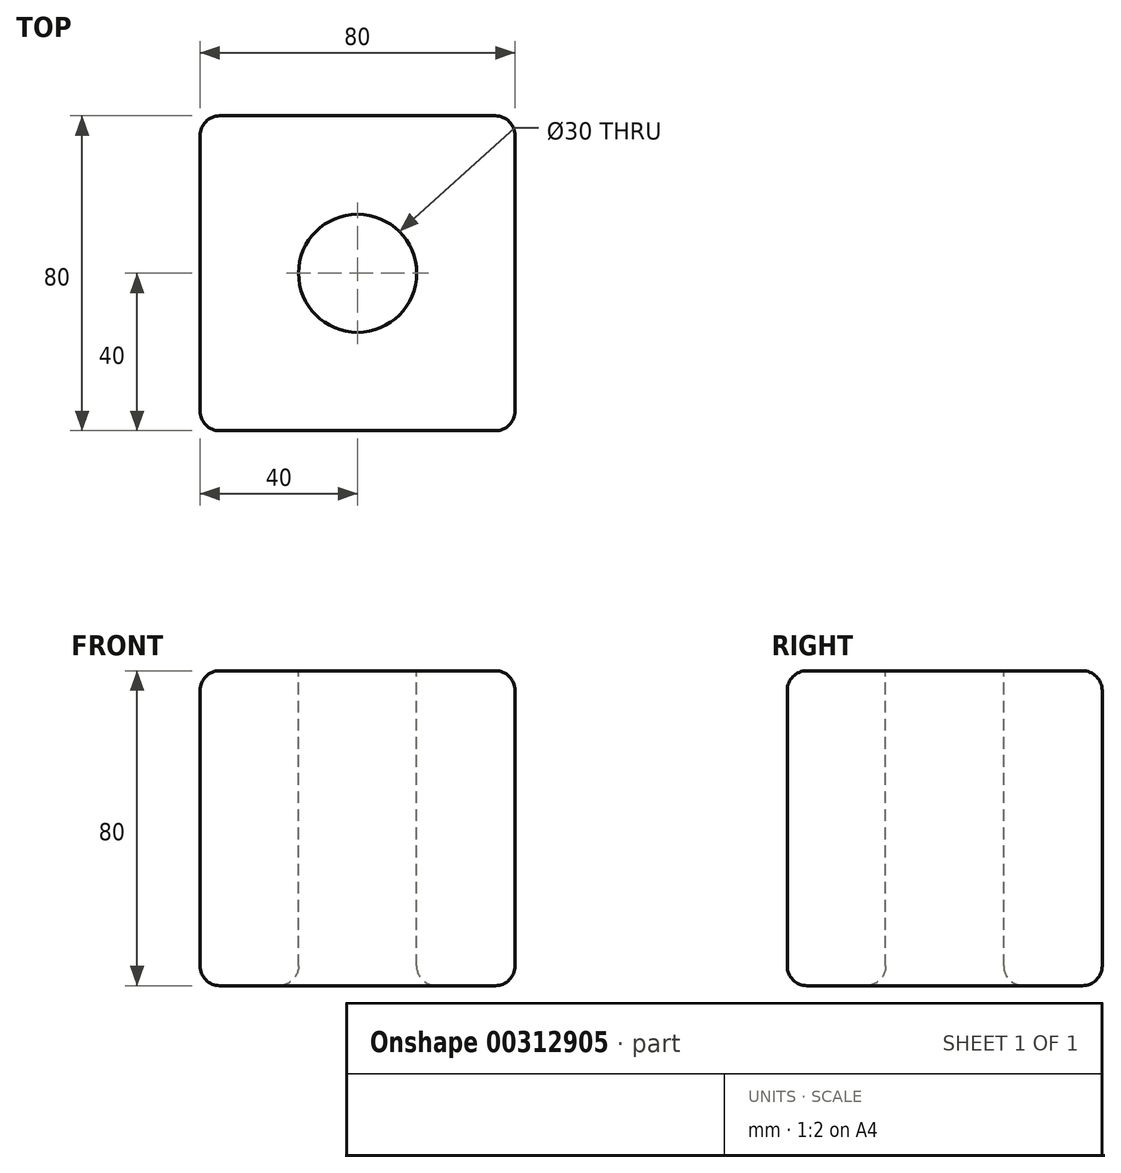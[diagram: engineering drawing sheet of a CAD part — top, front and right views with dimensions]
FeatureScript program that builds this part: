
annotation { "Feature Type Name" : "Feature", "Feature Type Description" : "" }
export const myFeature = defineFeature(function(context is Context, id is Id, definition is map)
    precondition{}
    {
        {
            var Q0;
            Q0=qCreatedBy(makeId("Top.planeOp"),FACE);
            var sketch = newSketch(context, id + "F0", { "sketchPlane" : qUnion([Q0])});
            skLineSegment(sketch, "E0.bottom", {"start": v(-40, 40) * mm, "end": v(40, 40) * mm});
            skLineSegment(sketch, "E0.top", {"start": v(-40, -40) * mm, "end": v(40, -40) * mm});
            skLineSegment(sketch, "E0.left", {"start": v(-40, 40) * mm, "end": v(-40, -40) * mm});
            skLineSegment(sketch, "E0.right", {"start": v(40, 40) * mm, "end": v(40, -40) * mm});
            skPoint(sketch, "E0.middle", {"position": v(0, 0) * mm});
            skSolve(sketch);
        }
        {
            var Q0;
            Q0 = qSketchRegion(id + "F0", true);
            extrude(context, id + "F1", {"entities" : qUnion([Q0]), "endBound" : BoundingType.SYMMETRIC, "depth" : 80 * mm});
        }
        {
            var Q0;
            Q0=makeQuery(id+"F1.opExtrude","CAP_FACE",FACE,{"disambiguationData":[OSD([sQuery(id+"F0.wireOp",EDGE,"E0.bottom"),sQuery(id+"F0.wireOp",EDGE,"E0.top"),sQuery(id+"F0.wireOp",EDGE,"E0.left"),sQuery(id+"F0.wireOp",EDGE,"E0.right")])],"isStart":false});
            var Q1;
            Q1=makeQuery(id+"F1.opExtrude","CAP_EDGE",EDGE,{"disambiguationData":[OSD([sQuery(id+"F0.wireOp",EDGE,"E0.left")])],"isStart":false});
            var Q2;
            Q2=makeQuery(id+"F1.opExtrude","CAP_EDGE",EDGE,{"disambiguationData":[OSD([sQuery(id+"F0.wireOp",EDGE,"E0.top")])],"isStart":false});
            var Q3;
            Q3=makeQuery(id+"F1.opExtrude","CAP_EDGE",EDGE,{"disambiguationData":[OSD([sQuery(id+"F0.wireOp",EDGE,"E0.right")])],"isStart":false});
            var Q4;
            Q4=makeQuery(id+"F1.opExtrude","CAP_EDGE",EDGE,{"disambiguationData":[OSD([sQuery(id+"F0.wireOp",EDGE,"E0.bottom")])],"isStart":false});
            var Q5;
            Q5=makeQuery(id+"F1.opExtrude","SWEPT_EDGE",EDGE,{"disambiguationData":[OSD([sQuery(id+"F0.wireOp",EDGE,"E0.bottom"),sQuery(id+"F0.wireOp",EDGE,"E0.left")])]});
            var Q6;
            Q6=makeQuery(id+"F1.opExtrude","SWEPT_EDGE",EDGE,{"disambiguationData":[OSD([sQuery(id+"F0.wireOp",EDGE,"E0.top"),sQuery(id+"F0.wireOp",EDGE,"E0.left")])]});
            var Q7;
            Q7=makeQuery(id+"F1.opExtrude","CAP_EDGE",EDGE,{"disambiguationData":[OSD([sQuery(id+"F0.wireOp",EDGE,"E0.bottom")])],"isStart":true});
            var Q8;
            Q8=makeQuery(id+"F1.opExtrude","CAP_EDGE",EDGE,{"disambiguationData":[OSD([sQuery(id+"F0.wireOp",EDGE,"E0.right")])],"isStart":true});
            var Q9;
            Q9=makeQuery(id+"F1.opExtrude","CAP_EDGE",EDGE,{"disambiguationData":[OSD([sQuery(id+"F0.wireOp",EDGE,"E0.top")])],"isStart":true});
            var Q10;
            Q10=makeQuery(id+"F1.opExtrude","CAP_EDGE",EDGE,{"disambiguationData":[OSD([sQuery(id+"F0.wireOp",EDGE,"E0.left")])],"isStart":true});
            var Q11;
            Q11=makeQuery(id+"F1.opExtrude","SWEPT_EDGE",EDGE,{"disambiguationData":[OSD([sQuery(id+"F0.wireOp",EDGE,"E0.bottom"),sQuery(id+"F0.wireOp",EDGE,"E0.right")])]});
            var Q12;
            Q12=makeQuery(id+"F1.opExtrude","SWEPT_EDGE",EDGE,{"disambiguationData":[OSD([sQuery(id+"F0.wireOp",EDGE,"E0.top"),sQuery(id+"F0.wireOp",EDGE,"E0.right")])]});
            fillet(context, id + "F2", {"entities" : qUnion([Q0, Q1, Q2, Q3, Q4, Q5, Q6, Q7, Q8, Q9, Q10, Q11, Q12]), "radius" : 5 * mm, "tangentPropagation" : true, "allowEdgeOverflow" : false});
        }
        {
            var Q0;
            Q0=makeQuery(id+"F1.opExtrude","CAP_FACE",FACE,{"disambiguationData":[OSD([sQuery(id+"F0.wireOp",EDGE,"E0.bottom"),sQuery(id+"F0.wireOp",EDGE,"E0.top"),sQuery(id+"F0.wireOp",EDGE,"E0.left"),sQuery(id+"F0.wireOp",EDGE,"E0.right")])],"isStart":false});
            var sketch = newSketch(context, id + "F3", { "sketchPlane" : qUnion([Q0])});
            skCircle(sketch, "E1", {"center": v(0, 0) * mm, "radius": 15 * mm});
            skSolve(sketch);
        }
        {
            var Q0;
            Q0=makeQuery(id+"F3.imprint","IMPRINT",FACE,{"disambiguationData":[TD([[makeQuery(id+"F3.imprint","IMPRINT",EDGE,{"derivedFrom":sQuery(id+"F3.wireOp",EDGE,"E1")}),1.0]])]});
            extrude(context, id + "F4", {"entities" : qUnion([Q0]), "operationType" : NewBodyOperationType.REMOVE, "endBound" : BoundingType.THROUGH_ALL, "oppositeDirection" : true, "depth" : 25 * mm});
        }
        {
            var Q0;
            Q0=makeQuery(id+"F4.boolean.opBoolean","COPY",EDGE,{"derivedFrom":makeQuery(id+"F4.opExtrude","CAP_EDGE",EDGE,{"disambiguationData":[OSD([sQuery(id+"F3.wireOp",EDGE,"E1")])],"isStart":true})});
            var Q1;
            Q1=makeQuery(id+"F4.boolean.opBoolean","INTERSECT",EDGE,{"derivedFrom":[makeQuery(id+"F1.opExtrude","CAP_FACE",FACE,{"disambiguationData":[OSD([sQuery(id+"F0.wireOp",EDGE,"E0.bottom"),sQuery(id+"F0.wireOp",EDGE,"E0.top"),sQuery(id+"F0.wireOp",EDGE,"E0.left"),sQuery(id+"F0.wireOp",EDGE,"E0.right")])],"isStart":true}),makeQuery(id+"F4.opExtrude","SWEPT_FACE",FACE,{"disambiguationData":[OSD([sQuery(id+"F3.wireOp",EDGE,"E1")])]})]});
            fillet(context, id + "F5", {"entities" : qUnion([Q0, Q1]), "radius" : 5 * mm, "tangentPropagation" : true, "allowEdgeOverflow" : false});
        }
    });
